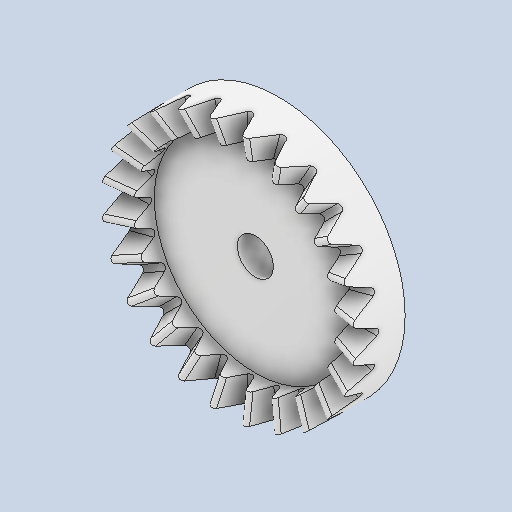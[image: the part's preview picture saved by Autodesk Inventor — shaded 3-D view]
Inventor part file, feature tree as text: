
AUTODESK INVENTOR PART (.ipt)
format: ipt  version: 2022.3 (Build 263350000, 350)  size: 433,664 bytes
history: native  units: mm
features: extrude x1, sketch x1, projected_geometry x1, imported_body x1
ambient origin geometry x8: Origin, YZ Plane, XZ Plane, XY Plane, X Axis, Y Axis, Z Axis, Center Point
bodies: Solid1 (feature_tree)
feature tree (4):
  extrude  "Extrusion1"  [1 undecoded]
  sketch  "Sketch1"  dims[d0=10.0mm d1=0.0mm]
  projected_geometry  "Projected Loop1"
  imported_body  "Base1"
note: 1 required parameter value undecoded (feature->parameter linkage not recoverable at this tier; creation-order binding heuristic only, values carry confidence <= 0.55)
